# Revit family: Access_Door-Best Access Doors-Contour-BA-UHF-MAG
name_source: partatom
category: Specialty Equipment
revit_build: Autodesk Revit 2017 (Build: 20160225_1515(x64)
units: mm (PartAtom-declared; Revit-internal decimal feet)

## family parameters
Cut with Voids When Loaded = No
Host = Face
OmniClass Number = 23.30.10.27.17
Part Type = Normal
Room Calculation Point = No
Round Connector Dimension = Use Diameter
Shared = No

## types (1)
- Not a Type - Load Type Catalog
    Actual Height = 29"
    Actual Width = 16"
    Assembly Code = C1020700
    Construction Material = Metal - Best Access Doors - Aluminum
    Default Elevation = 0"
    Description = Access door with hidden Flange & Latch
    Finish = Metal - Best Access Doors - Powder Coated White
    Frame Depth = 1 113/256"
    Height = 29"
    Height C = 29"
    Manufacturer = Best Access Doors
    Model = BA-UHF-MAG
    Neoprene Gasket = No
    Neoprene Gasket Material = Neoprene - Best Access Doors -  Gasket
    Product data url = https://bimobject.com
    Type Comments = Please Load Accompanying .txt File
    URL = http://www.bestaccessdoors.com
    Version = 2015 V1.0m
    Width = 16"
    Width C = 16"

## geometry (parser evidence)
native form markers: Blend x4, Sweep x5
no freeform markers — native parametric forms only
